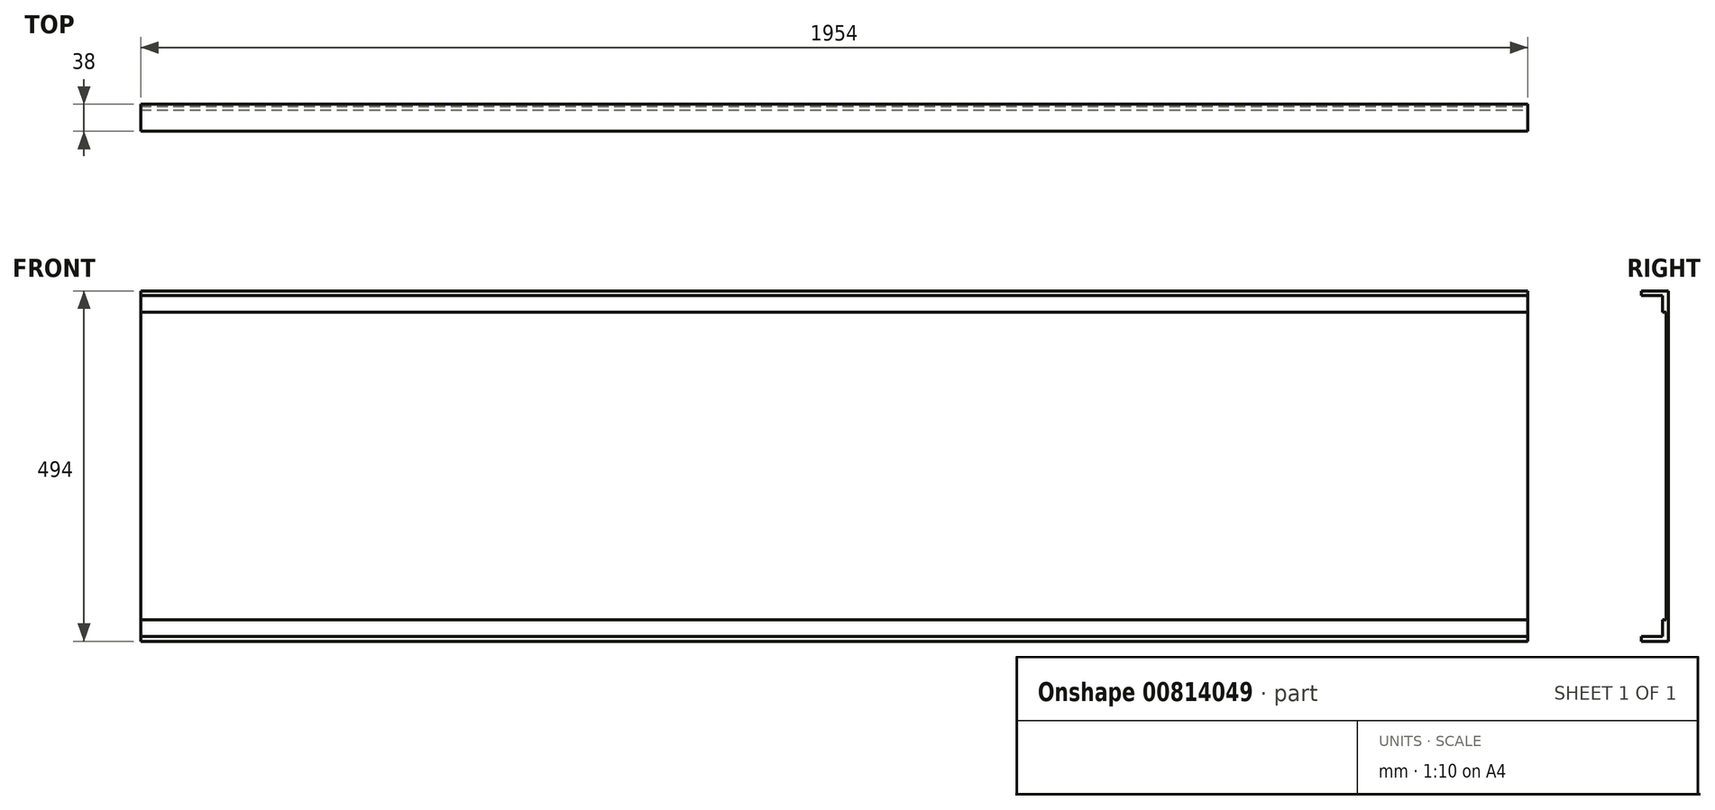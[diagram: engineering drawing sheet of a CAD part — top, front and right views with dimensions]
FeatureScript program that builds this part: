
annotation { "Feature Type Name" : "Feature", "Feature Type Description" : "" }
export const myFeature = defineFeature(function(context is Context, id is Id, definition is map)
    precondition{}
    {
        {
            var Q0;
            Q0=qCreatedBy(makeId("Front.planeOp"),FACE);
            var sketch = newSketch(context, id + "F0", { "sketchPlane" : qUnion([Q0])});
            skLineSegment(sketch, "E0.bottom", {"start": v(-977, 247) * mm, "end": v(977, 247) * mm});
            skLineSegment(sketch, "E0.top", {"start": v(-977, -247) * mm, "end": v(977, -247) * mm});
            skLineSegment(sketch, "E0.left", {"start": v(-977, 247) * mm, "end": v(-977, -247) * mm});
            skLineSegment(sketch, "E0.right", {"start": v(977, 247) * mm, "end": v(977, -247) * mm});
            skPoint(sketch, "E0.middle", {"position": v(0, 0) * mm});
            skLineSegment(sketch, "E1", {"start": v(0, -247) * mm, "end": v(0, 247) * mm, "construction": true});
            skLineSegment(sketch, "E2", {"start": v(977, 0) * mm, "end": v(-977, 0) * mm, "construction": true});
            skLineSegment(sketch, "E3", {"start": v(500, 247) * mm, "end": v(500, -247) * mm, "construction": true});
            skLineSegment(sketch, "E4", {"start": v(-500, 247) * mm, "end": v(-500, -247) * mm, "construction": true});
            skLineSegment(sketch, "E5", {"start": v(1000, 330.01) * mm, "end": v(1000, -320.46) * mm, "construction": true});
            skLineSegment(sketch, "E6", {"start": v(-1000, 314.94) * mm, "end": v(-1000, -353.1) * mm, "construction": true});
            skLineSegment(sketch, "E7", {"start": v(0, 0) * mm, "end": v(-1109.63, 0) * mm, "construction": true});
            skLineSegment(sketch, "E8", {"start": v(-1109.63, 0) * mm, "end": v(1276.26, 0) * mm, "construction": true});
            skLineSegment(sketch, "E9", {"start": v(-1132.23, 217) * mm, "end": v(1278.78, 217) * mm, "construction": true});
            skLineSegment(sketch, "E10", {"start": v(-1137.25, -217) * mm, "end": v(1281.29, -217) * mm, "construction": true});
            skSolve(sketch);
        }
        {
            var Q0;
            Q0 = qSketchRegion(id + "F0", true);
            extrude(context, id + "F1", {"entities" : qUnion([Q0]), "depth" : 3 * mm, "offsetDistance" : 25 * mm});
        }
        {
            var Q0;
            Q0=makeQuery(id+"F1.opExtrude","CAP_FACE",FACE,{"disambiguationData":[OSD([sQuery(id+"F0.wireOp",EDGE,"E0.bottom"),sQuery(id+"F0.wireOp",EDGE,"E0.top"),sQuery(id+"F0.wireOp",EDGE,"E0.left"),sQuery(id+"F0.wireOp",EDGE,"E0.right")])],"isStart":false});
            var sketch = newSketch(context, id + "F2", { "sketchPlane" : qUnion([Q0])});
            skLineSegment(sketch, "E11.bottom", {"start": v(-977, 247) * mm, "end": v(977, 247) * mm});
            skLineSegment(sketch, "E11.top", {"start": v(-977, 217) * mm, "end": v(977, 217) * mm});
            skLineSegment(sketch, "E11.left", {"start": v(-977, 247) * mm, "end": v(-977, 217) * mm});
            skLineSegment(sketch, "E11.right", {"start": v(977, 247) * mm, "end": v(977, 217) * mm});
            skLineSegment(sketch, "E12.MirrorCS", {"start": v(977, -247) * mm, "end": v(977, -217) * mm});
            skLineSegment(sketch, "E13.MirrorCS", {"start": v(-977, -247) * mm, "end": v(-977, -217) * mm});
            skLineSegment(sketch, "E14.MirrorCS", {"start": v(-977, -217) * mm, "end": v(977, -217) * mm});
            skLineSegment(sketch, "E15.MirrorCS", {"start": v(-977, -247) * mm, "end": v(977, -247) * mm});
            skSolve(sketch);
        }
        {
            var Q0;
            Q0 = qSketchRegion(id + "F2", true);
            extrude(context, id + "F3", {"entities" : qUnion([Q0]), "operationType" : NewBodyOperationType.ADD, "depth" : 5 * mm, "offsetDistance" : 25 * mm});
        }
        {
            var Q0;
            Q0=makeQuery(id+"F3.opExtrude","CAP_FACE",FACE,{"disambiguationData":[OSD([sQuery(id+"F2.wireOp",EDGE,"E11.bottom"),sQuery(id+"F2.wireOp",EDGE,"E11.top"),sQuery(id+"F2.wireOp",EDGE,"E11.left"),sQuery(id+"F2.wireOp",EDGE,"E11.right")])],"isStart":false});
            var sketch = newSketch(context, id + "F4", { "sketchPlane" : qUnion([Q0])});
            skLineSegment(sketch, "E16.bottom", {"start": v(-977, 247) * mm, "end": v(977, 247) * mm});
            skLineSegment(sketch, "E16.top", {"start": v(-977, 240.38) * mm, "end": v(977, 240.38) * mm});
            skLineSegment(sketch, "E16.left", {"start": v(-977, 247) * mm, "end": v(-977, 240.38) * mm});
            skLineSegment(sketch, "E16.right", {"start": v(977, 247) * mm, "end": v(977, 240.38) * mm});
            skLineSegment(sketch, "E17.MirrorCS", {"start": v(977, -247) * mm, "end": v(977, -240.38) * mm});
            skLineSegment(sketch, "E18.MirrorCS", {"start": v(-977, -247) * mm, "end": v(-977, -240.38) * mm});
            skLineSegment(sketch, "E19.MirrorCS", {"start": v(-977, -240.38) * mm, "end": v(977, -240.38) * mm});
            skLineSegment(sketch, "E20.MirrorCS", {"start": v(-977, -247) * mm, "end": v(977, -247) * mm});
            skSolve(sketch);
        }
        {
            var Q0;
            Q0 = qSketchRegion(id + "F4", true);
            extrude(context, id + "F5", {"entities" : qUnion([Q0]), "operationType" : NewBodyOperationType.ADD, "depth" : 30 * mm, "offsetDistance" : 25 * mm});
        }
    });
